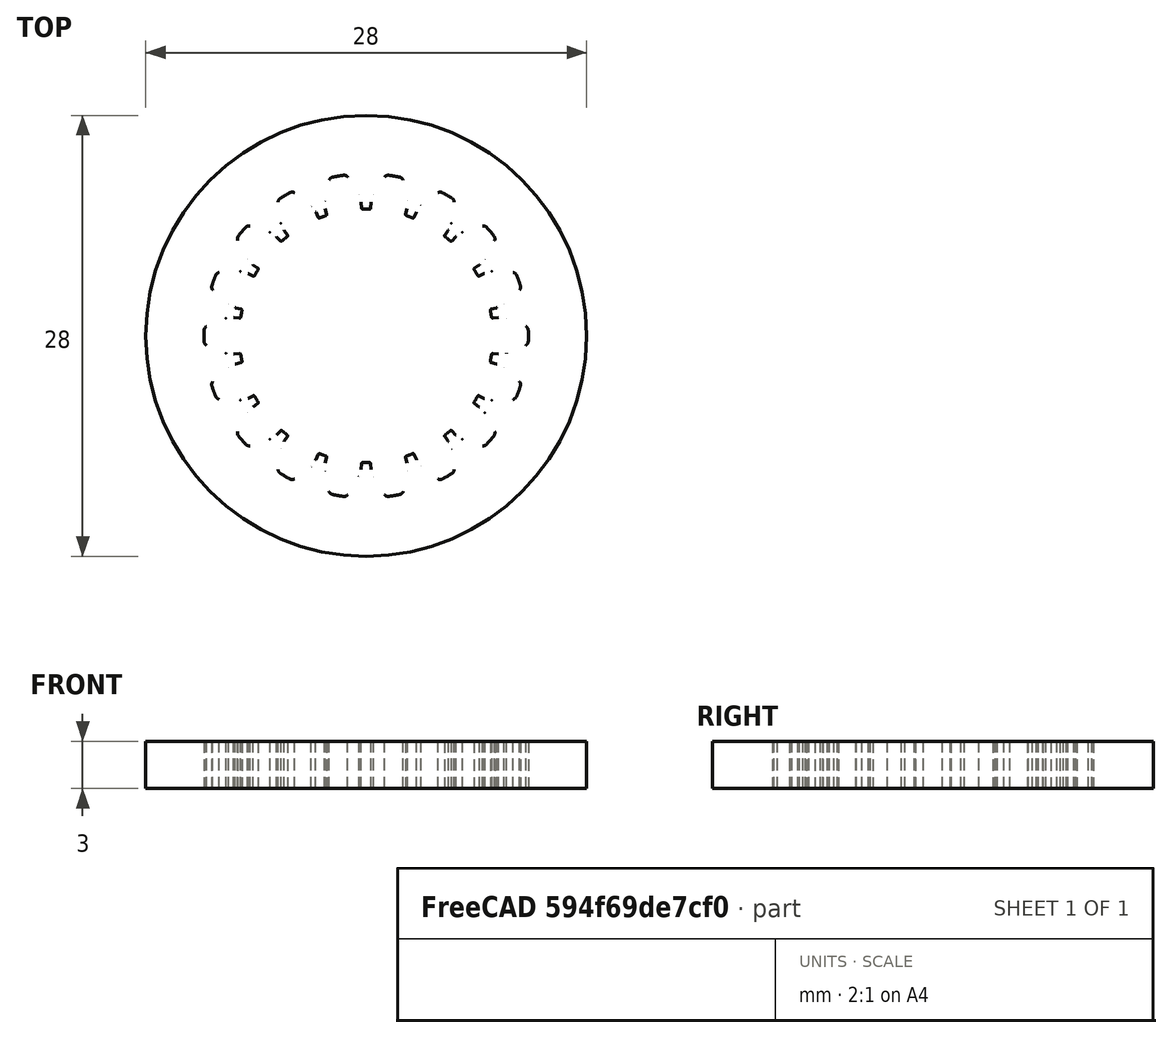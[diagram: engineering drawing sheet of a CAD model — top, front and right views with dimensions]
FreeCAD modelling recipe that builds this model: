
FCSTD DOCUMENT  (FreeCAD 0.19R24276 (Git))
Label: Gear_privod_perehodnik_to_GT2_test_3mm_offset_03_A2
License: All rights reserved
LicenseURL: http://en.wikipedia.org/wiki/All_rights_reserved
objects: Part::Part2DObjectPython×1, Part::Offset2D×1, Part::FeaturePython×1
note: 3 computed .brp shape members not serialized (recipe doc carries the construction recipe); baked Part::Feature solids carry a one-line shape summary decoded from their .brp

FEATURE [Part::Part2DObjectPython] InvoluteGear  # Draft 2D object (typed FeaturePython)
  ExternalGear = true
  HighPrecision = true
  Modules = 1
  NumberOfTeeth = 18
  PressureAngle = 20
FEATURE [Part::Offset2D] Offset2D
  Fill = false
  Intersection = false
  Join = 0
  Mode = 1
  SelfIntersection = false
  Source = -> InvoluteGear
  Value = 0.3
FEATURE [Part::FeaturePython] b_Gear_privod_perehodnik_to_GT2_test_3mm_offset_03_001_  label="Gear_privod_perehodnik_to_GT2_test_3mm_offset_03_001"  # a2plus imported part (geometry in sourceFile) (typed FeaturePython)
  a2p_Version = V0.1
  fixedPosition = true
  objectType = a2pPart
  sourceFile = .\Gear_privod_perehodnik_to_GT2_test_3mm_offset_03.FCStd
  subassemblyImport = false
  timeLastImport = 1.64791e+09
  updateColors = true
